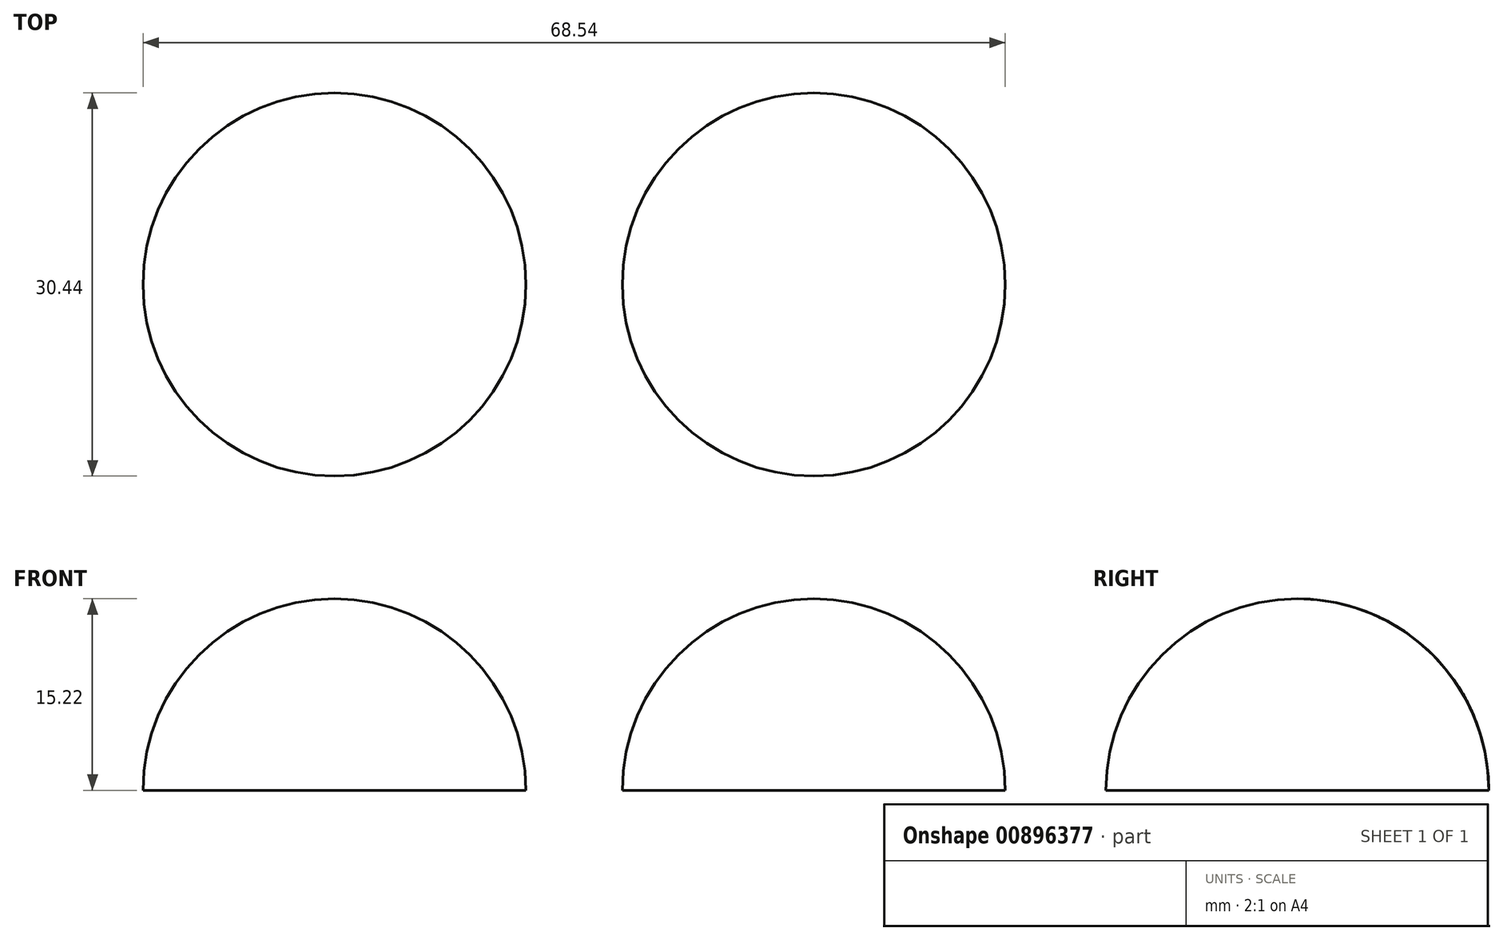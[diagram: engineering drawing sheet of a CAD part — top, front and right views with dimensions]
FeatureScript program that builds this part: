
annotation { "Feature Type Name" : "Feature", "Feature Type Description" : "" }
export const myFeature = defineFeature(function(context is Context, id is Id, definition is map)
    precondition{}
    {
        {
            var Q0;
            Q0=qCreatedBy(makeId("Right.planeOp"),FACE);
            var sketch = newSketch(context, id + "F0", { "sketchPlane" : qUnion([Q0])});
            skLineSegment(sketch, "E0", {"start": v(0, 0) * mm, "end": v(0, 15.22) * mm});
            skArc(sketch, "E1", {"start": v(15.22, 0) * mm, "mid": v(10.76, 10.76) * mm, "end": v(0, 15.22) * mm});
            skLineSegment(sketch, "E2", {"start": v(0, 0) * mm, "end": v(15.22, 0) * mm});
            skSolve(sketch);
        }
        {
            var Q0;
            Q0 = qSketchRegion(id + "F0", true);
            var Q1;
            Q1=sQuery(id+"F0.wireOp",EDGE,"E0");
            revolve(context, id + "F1", {"surfaceOperationType" : NewSurfaceOperationType.NEW, "entities" : qUnion([Q0]), "axis" : qUnion([Q1]), "revolveType" : RevolveType.FULL});
        }
        {
            var Q0;
            Q0=makeQuery(id+"F1.opRevolve","SWEPT_BODY",BODY,{"disambiguationData":[OSD([sQuery(id+"F0.wireOp",EDGE,"E0"),sQuery(id+"F0.wireOp",EDGE,"E1"),sQuery(id+"F0.wireOp",EDGE,"E2")])]});
            transform(context, id + "F2", {"entities" : qUnion([Q0]), "transformType" : TransformType.TRANSLATION_3D, "dx" : 38.1 * mm, "dy" : 0 * mm, "dz" : 0 * mm, "makeCopy" : true});
        }
    });
